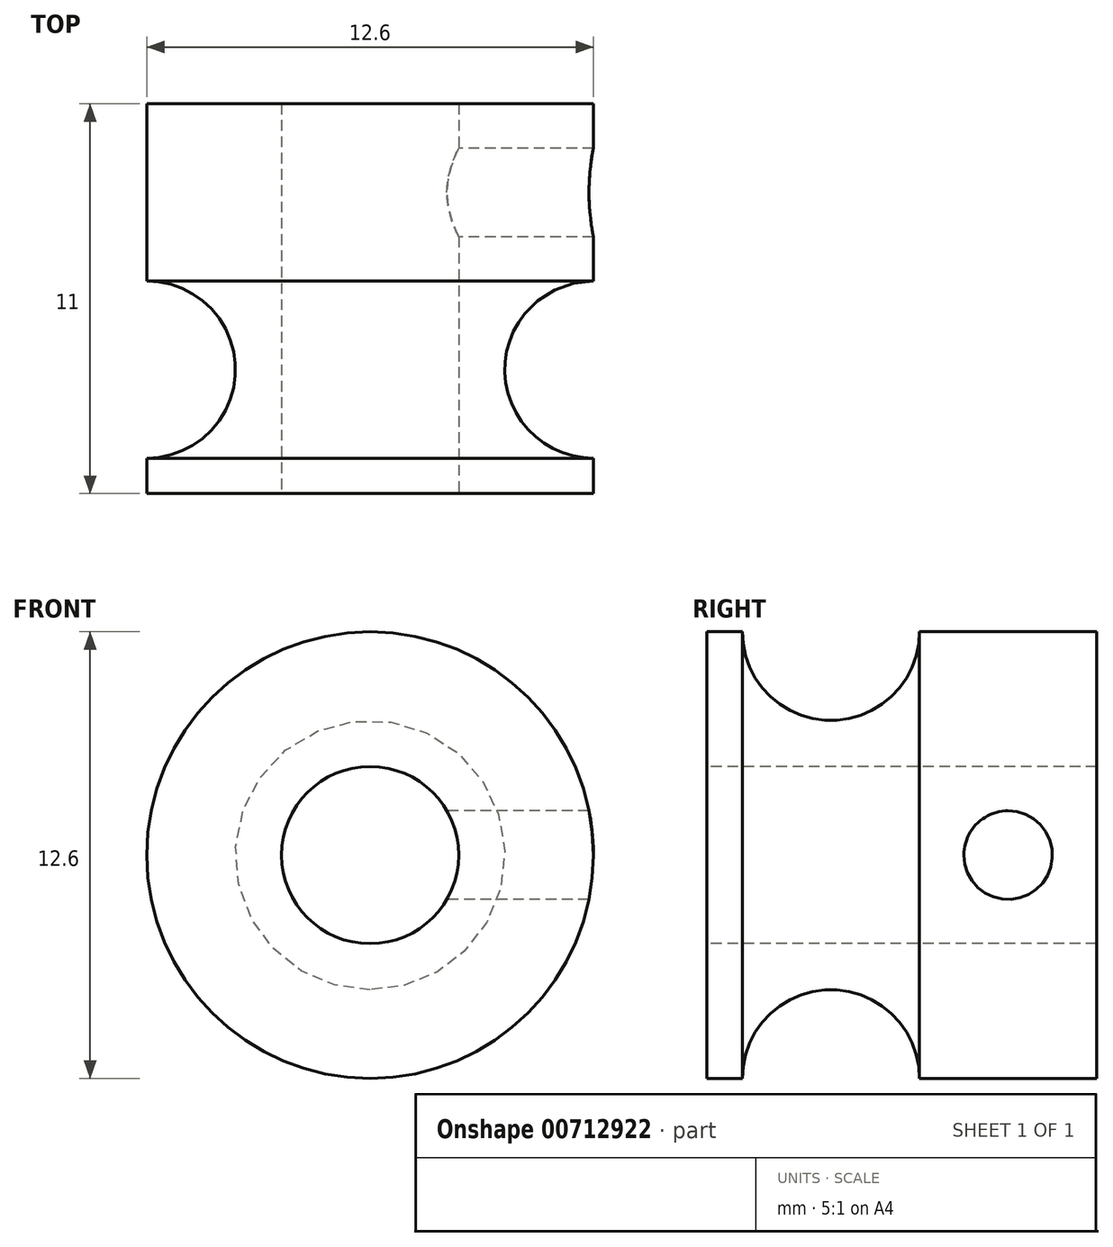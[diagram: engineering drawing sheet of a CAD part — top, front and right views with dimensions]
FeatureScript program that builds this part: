
annotation { "Feature Type Name" : "Feature", "Feature Type Description" : "" }
export const myFeature = defineFeature(function(context is Context, id is Id, definition is map)
    precondition{}
    {
        {
            var Q0;
            Q0=qCreatedBy(makeId("Front.planeOp"),FACE);
            var sketch = newSketch(context, id + "F0", { "sketchPlane" : qUnion([Q0])});
            skCircle(sketch, "E0", {"center": v(0, 0) * mm, "radius": 6.3 * mm});
            skCircle(sketch, "E1", {"center": v(0, 0) * mm, "radius": 5.2 * mm, "construction": true});
            skCircle(sketch, "E2", {"center": v(0, 0) * mm, "radius": 2.5 * mm});
            skSolve(sketch);
        }
        {
            var Q0;
            Q0=makeQuery(id+"F0.imprint","IMPRINT",FACE,{"disambiguationData":[TD([[makeQuery(id+"F0.imprint","IMPRINT",EDGE,{"derivedFrom":sQuery(id+"F0.wireOp",EDGE,"E0")}),1.0]])]});
            extrude(context, id + "F1", {"entities" : qUnion([Q0]), "oppositeDirection" : true, "depth" : 5 * mm, "offsetDistance" : 25 * mm, "hasSecondDirection" : true, "secondDirectionOppositeDirection" : false, "secondDirectionDepth" : 6 * mm});
        }
        {
            var Q0;
            Q0=qCreatedBy(makeId("Right.planeOp"),FACE);
            var sketch = newSketch(context, id + "F2", { "sketchPlane" : qUnion([Q0])});
            skLineSegment(sketch, "E3", {"start": v(-6, 6.3) * mm, "end": v(5, 6.3) * mm});
            skCircle(sketch, "E4", {"center": v(-2.5, 6.3) * mm, "radius": 2.5 * mm});
            skPoint(sketch, "E5", {"position": v(2.5, 0) * mm});
            skSolve(sketch);
        }
        {
            var Q0;
            {var subQ0=sQuery(id+"F2.wireOp",EDGE,"E4");var subQ1=sQuery(id+"F2.wireOp",EDGE,"E3");var subQ2=makeQuery(id+"F2.imprint","INTERSECT",VERTEX,{"disambiguationData":[OD(0.0)],"derivedFrom":[subQ1,subQ0]});Q0=makeQuery(id+"F2.imprint","IMPRINT",FACE,{"disambiguationData":[TD([[makeQuery(id+"F2.imprint","IMPRINT",EDGE,{"disambiguationData":[TD([[subQ2,-1.0]])],"derivedFrom":subQ1}),1.0]])]});}
            var Q1;
            {var subQ0=sQuery(id+"F2.wireOp",EDGE,"E4");var subQ1=sQuery(id+"F2.wireOp",EDGE,"E3");var subQ2=makeQuery(id+"F2.imprint","INTERSECT",VERTEX,{"disambiguationData":[OD(0.0)],"derivedFrom":[subQ1,subQ0]});Q1=makeQuery(id+"F2.imprint","IMPRINT",FACE,{"disambiguationData":[TD([[makeQuery(id+"F2.imprint","IMPRINT",EDGE,{"disambiguationData":[TD([[subQ2,-1.0]])],"derivedFrom":subQ1}),-1.0]])]});}
            var Q2;
            Q2=makeQuery(id+"F1.opExtrude","CAP_EDGE",EDGE,{"disambiguationData":[OSD([sQuery(id+"F0.wireOp",EDGE,"E0")])],"isStart":true});
            revolve(context, id + "F3", {"operationType" : NewBodyOperationType.REMOVE, "surfaceOperationType" : NewSurfaceOperationType.NEW, "entities" : qUnion([Q0, Q1]), "axis" : qUnion([Q2]), "revolveType" : RevolveType.FULL, "oppositeDirection" : true});
        }
        {
            var Q0;
            Q0=qCreatedBy(makeId("Right.planeOp"),FACE);
            cPlane(context, id + "F4", {"entities" : qUnion([Q0]), "cplaneType" : CPlaneType.OFFSET, "offset" : (12.6 / 2) * mm, "width" : 150 * mm, "height" : 150 * mm});
        }
        {
            var Q0;
            Q0=qCreatedBy(id+"F4.planeOp",FACE);
            var sketch = newSketch(context, id + "F5", { "sketchPlane" : qUnion([Q0])});
            skPoint(sketch, "E6", {"position": v(2.5, 0) * mm});
            skSolve(sketch);
        }
        {
            var Q0;
            Q0=sQuery(id+"F5.wireOp",VERTEX,"E6");
            var Q1;
            Q1=makeQuery(id+"F1.opExtrude","SWEPT_BODY",BODY,{"disambiguationData":[OSD([sQuery(id+"F0.wireOp",EDGE,"E0"),sQuery(id+"F0.wireOp",EDGE,"E2")])]});
            hole(context, id + "F6", {"style" : HoleStyle.SIMPLE, "endStyle" : HoleEndStyle.BLIND, "holeDiameter" : 2.5 * mm, "majorDiameter" : 5 * mm, "holeDepth" : 5 * mm, "isTappedThrough" : true, "tappedDepth" : 12 * mm, "tapClearance" : 3, "locations" : qUnion([Q0]), "scope" : qUnion([Q1]), "startStyle" : HoleStartStyle.PART});
        }
    });
